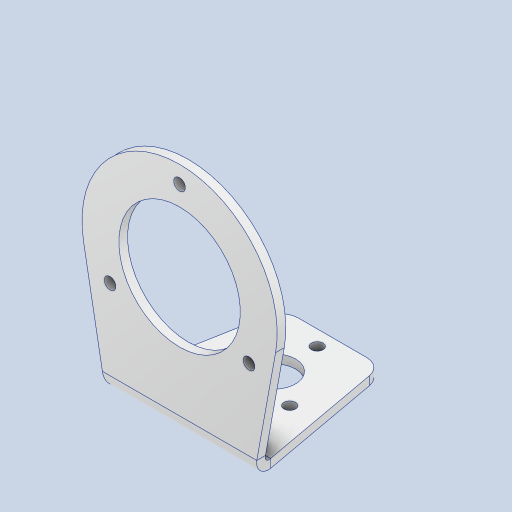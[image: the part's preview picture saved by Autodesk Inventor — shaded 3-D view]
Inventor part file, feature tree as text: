
AUTODESK INVENTOR PART (.ipt)
format: ipt  version: 2023 (Build 270158000, 158)  size: 282,112 bytes
history: native  units: mm
features: other x7, fillet x1, sketch x1
ambient origin geometry x8: Origin, YZ Plane, XZ Plane, XY Plane, X Axis, Y Axis, Z Axis, Center Point
bodies: Body1 (feature_tree), Body2 (feature_tree)
feature tree (9):
  other  "GIM3505-8_with-driver.ipt"
  other  "ソリッド1"
  other  "折り曲げ1"
  fillet  "フィレット1"  Radius=10.0mm
  other  "TaggingFeature1"
  other  "プレート1"
  sketch  "スケッチ2"
  other  "ソリッド1::GIM3505-8_with-driver.ipt"
  other  "Srf1"
